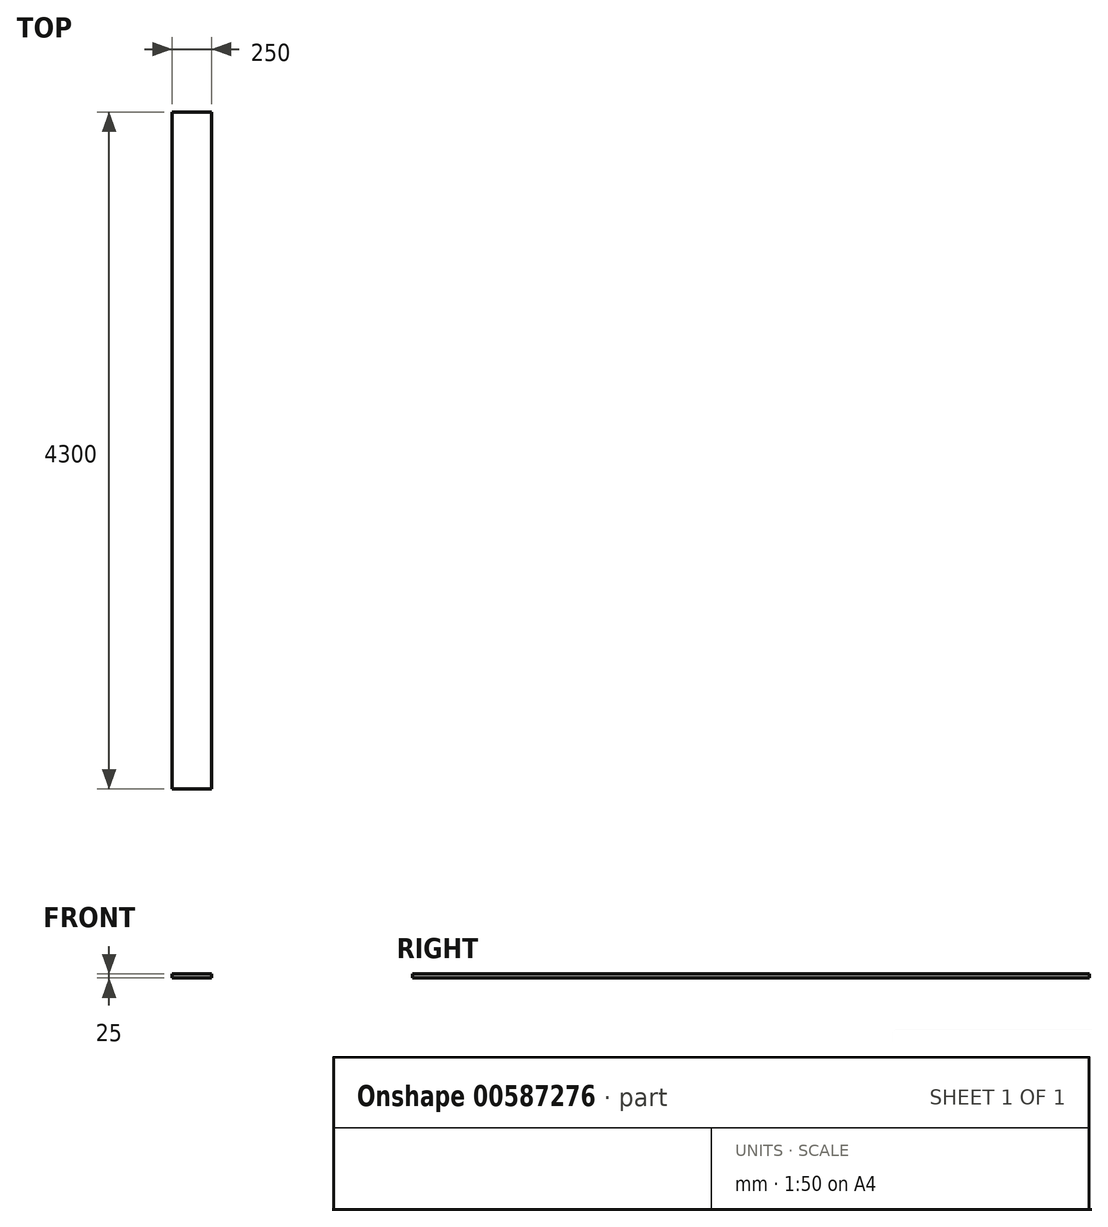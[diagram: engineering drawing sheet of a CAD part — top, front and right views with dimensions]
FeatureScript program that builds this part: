
annotation { "Feature Type Name" : "Feature", "Feature Type Description" : "" }
export const myFeature = defineFeature(function(context is Context, id is Id, definition is map)
    precondition{}
    {
        {
            var Q0;
            Q0=qCreatedBy(makeId("Top.planeOp"),FACE);
            var sketch = newSketch(context, id + "F0", { "sketchPlane" : qUnion([Q0])});
            skLineSegment(sketch, "E0.bottom", {"start": v(125, 2150) * mm, "end": v(-125, 2150) * mm});
            skLineSegment(sketch, "E0.top", {"start": v(125, -2150) * mm, "end": v(-125, -2150) * mm});
            skLineSegment(sketch, "E0.left", {"start": v(125, 2150) * mm, "end": v(125, -2150) * mm});
            skLineSegment(sketch, "E0.right", {"start": v(-125, 2150) * mm, "end": v(-125, -2150) * mm});
            skPoint(sketch, "E0.middle", {"position": v(0, 0) * mm});
            skSolve(sketch);
        }
        {
            var Q0;
            Q0=makeQuery(id+"F0.imprint","IMPRINT",FACE,{"disambiguationData":[TD([[makeQuery(id+"F0.imprint","IMPRINT",EDGE,{"derivedFrom":sQuery(id+"F0.wireOp",EDGE,"E0.bottom")}),1.0]])]});
            extrude(context, id + "F1", {"entities" : qUnion([Q0]), "depth" : 25 * mm, "offsetDistance" : 25 * mm});
        }
    });
